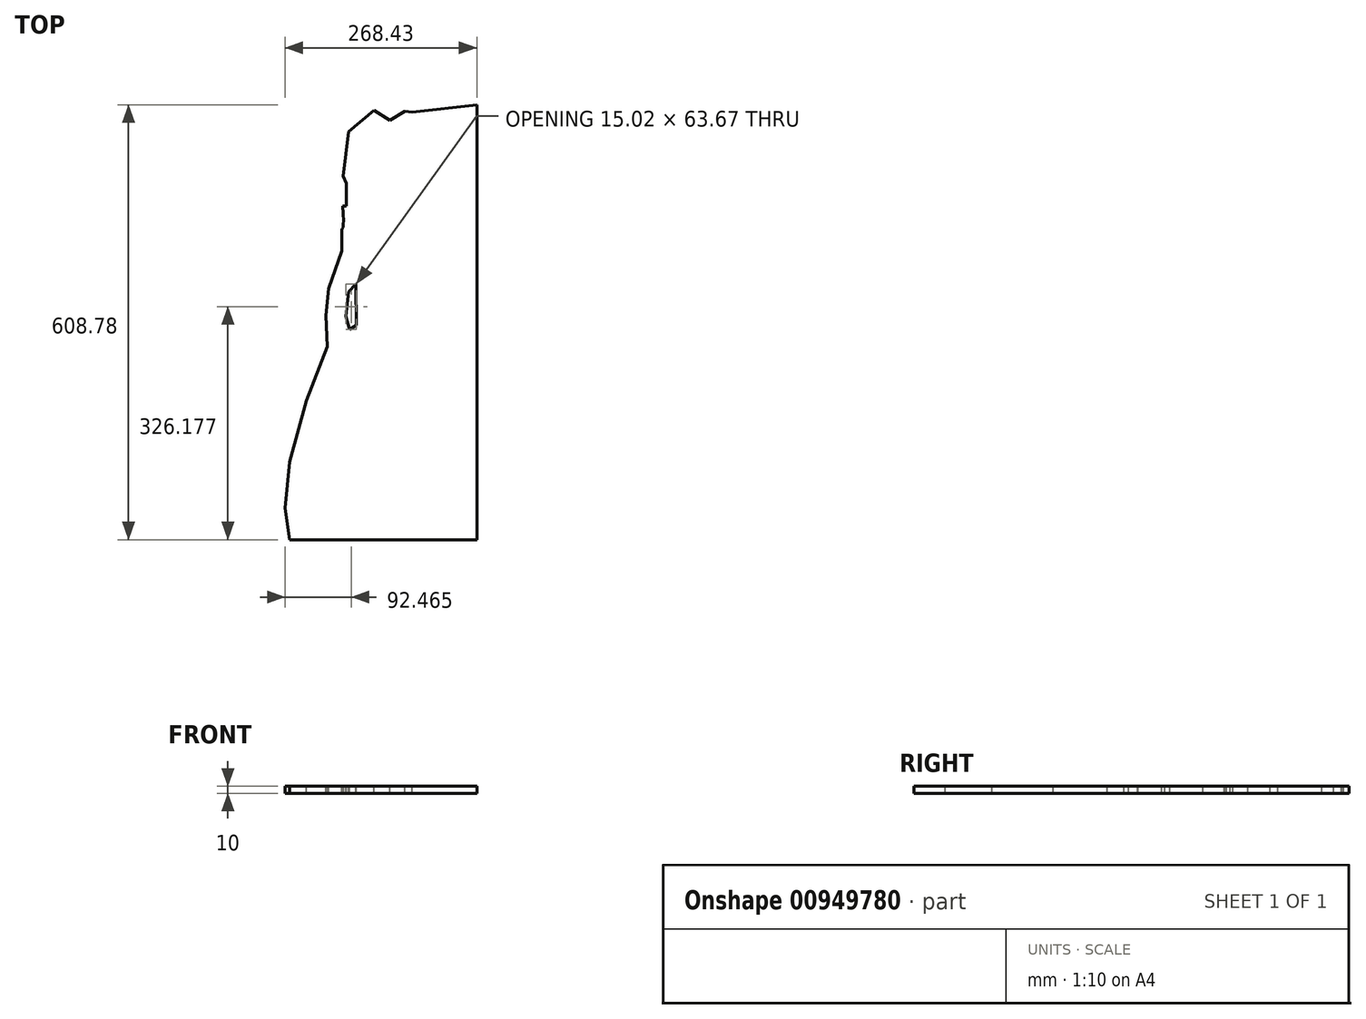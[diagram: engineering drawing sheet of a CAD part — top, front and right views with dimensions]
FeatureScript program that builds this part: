
annotation { "Feature Type Name" : "Feature", "Feature Type Description" : "" }
export const myFeature = defineFeature(function(context is Context, id is Id, definition is map)
    precondition{}
    {
        {
            var Q0;
            Q0=qCreatedBy(makeId("Top.planeOp"),FACE);
            var sketch = newSketch(context, id + "F0", { "sketchPlane" : qUnion([Q0])});
            skLineSegment(sketch, "E0", {"start": v(0, 0) * mm, "end": v(0, 507.42) * mm});
            skLineSegment(sketch, "E1", {"start": v(0, 0) * mm, "end": v(0, -560.7) * mm});
            skLineSegment(sketch, "E2", {"start": v(0, 266.98) * mm, "end": v(-90.5, 256.7) * mm});
            skLineSegment(sketch, "E3", {"start": v(-90.5, 256.7) * mm, "end": v(-100.8, 258.43) * mm});
            skLineSegment(sketch, "E4", {"start": v(-100.8, 258.43) * mm, "end": v(-121.81, 245.63) * mm});
            skLineSegment(sketch, "E5", {"start": v(-121.81, 245.63) * mm, "end": v(-143.96, 259.3) * mm});
            skLineSegment(sketch, "E6", {"start": v(-143.96, 259.3) * mm, "end": v(-179.77, 229.36) * mm});
            skLineSegment(sketch, "E7", {"start": v(-179.77, 229.36) * mm, "end": v(-187.05, 167.53) * mm});
            skLineSegment(sketch, "E8", {"start": v(-187.05, 167.53) * mm, "end": v(-182.93, 157.04) * mm});
            skLineSegment(sketch, "E9", {"start": v(-182.93, 157.04) * mm, "end": v(-182.93, 125.57) * mm});
            skLineSegment(sketch, "E10", {"start": v(-182.93, 125.57) * mm, "end": v(-188, 125.57) * mm});
            skLineSegment(sketch, "E11", {"start": v(-188, 125.57) * mm, "end": v(-187.05, 114.34) * mm});
            skLineSegment(sketch, "E12", {"start": v(-187.05, 114.34) * mm, "end": v(-186.28, 104.53) * mm});
            skLineSegment(sketch, "E13", {"start": v(-186.28, 104.53) * mm, "end": v(-187.05, 100.89) * mm});
            skLineSegment(sketch, "E14", {"start": v(-187.05, 100.89) * mm, "end": v(-187.05, 95.58) * mm});
            skLineSegment(sketch, "E15", {"start": v(-187.05, 95.58) * mm, "end": v(-188.28, 93.74) * mm});
            skLineSegment(sketch, "E16", {"start": v(-189.28, 62.57) * mm, "end": v(-189.28, 92.41) * mm});
            skLineSegment(sketch, "E17", {"start": v(-189.28, 92.41) * mm, "end": v(-188.28, 93.74) * mm});
            skLineSegment(sketch, "E18", {"start": v(-189.28, 62.57) * mm, "end": v(-207.18, 9.6) * mm});
            skLineSegment(sketch, "E19", {"start": v(-207.18, 9.6) * mm, "end": v(-211.46, -27.83) * mm});
            skLineSegment(sketch, "E20", {"start": v(-211.46, -27.83) * mm, "end": v(-209.5, -71.38) * mm});
            skLineSegment(sketch, "E21", {"start": v(-209.5, -71.38) * mm, "end": v(-238.46, -147.05) * mm});
            skLineSegment(sketch, "E22", {"start": v(-238.46, -147.05) * mm, "end": v(-262.31, -232.57) * mm});
            skLineSegment(sketch, "E23", {"start": v(-262.31, -232.57) * mm, "end": v(-268.43, -297.65) * mm});
            skLineSegment(sketch, "E24", {"start": v(-268.43, -297.65) * mm, "end": v(-262.31, -341.8) * mm});
            skLineSegment(sketch, "E25", {"start": v(-262.31, -341.8) * mm, "end": v(0, -341.8) * mm});
            skArc(sketch, "E26", {"start": v(0, 183.04) * mm, "mid": v(-31.78, 179.78) * mm, "end": v(-63.3, 174.56) * mm});
            skLineSegment(sketch, "E27", {"start": v(-63.3, 174.56) * mm, "end": v(-90.15, 159.72) * mm});
            skLineSegment(sketch, "E28", {"start": v(-90.15, 159.72) * mm, "end": v(-110.08, 125.1) * mm});
            skLineSegment(sketch, "E29", {"start": v(-110.08, 125.1) * mm, "end": v(-117.57, 112.44) * mm});
            skLineSegment(sketch, "E30", {"start": v(-117.57, 112.44) * mm, "end": v(-121.54, 81.78) * mm});
            skLineSegment(sketch, "E31", {"start": v(-118.27, 18.78) * mm, "end": v(-121.54, 81.78) * mm});
            skLineSegment(sketch, "E32", {"start": v(-118.27, 18.78) * mm, "end": v(-91.05, -12.19) * mm});
            skLineSegment(sketch, "E33", {"start": v(-91.05, -12.19) * mm, "end": v(-67.19, -36.05) * mm});
            skLineSegment(sketch, "E34", {"start": v(-67.19, -36.05) * mm, "end": v(-44.56, -45.31) * mm});
            skLineSegment(sketch, "E35", {"start": v(-44.56, -45.31) * mm, "end": v(0, -56) * mm});
            skLineSegment(sketch, "E36", {"start": v(-169.38, 16.21) * mm, "end": v(-179.36, 5.2) * mm});
            skLineSegment(sketch, "E37", {"start": v(-179.36, 5.2) * mm, "end": v(-183.47, -28.84) * mm});
            skLineSegment(sketch, "E38", {"start": v(-183.47, -28.84) * mm, "end": v(-178.54, -47.46) * mm});
            skLineSegment(sketch, "E39", {"start": v(-178.54, -47.46) * mm, "end": v(-168.46, -41.7) * mm});
            skLineSegment(sketch, "E40", {"start": v(-168.46, -41.7) * mm, "end": v(-169.38, 16.21) * mm});
            skLineSegment(sketch, "E41", {"start": v(-44.56, 261.84) * mm, "end": v(-91.08, 211.7) * mm});
            skPoint(sketch, "E41.startSnap0", {"position": v(-45.25, 261.84) * mm});
            skLineSegment(sketch, "E42", {"start": v(-91.08, 211.7) * mm, "end": v(-91.08, 200.93) * mm});
            skLineSegment(sketch, "E43", {"start": v(-91.08, 200.93) * mm, "end": v(0, 200.93) * mm});
            skLineSegment(sketch, "E44", {"start": v(0, 200.93) * mm, "end": v(-44.56, 261.84) * mm});
            skLineSegment(sketch, "E45", {"start": v(-153.96, 177.08) * mm, "end": v(-128.27, 176.1) * mm});
            skLineSegment(sketch, "E46", {"start": v(-128.27, 176.1) * mm, "end": v(-128.27, 162.4) * mm});
            skLineSegment(sketch, "E47", {"start": v(-128.27, 162.4) * mm, "end": v(-155.67, 161.42) * mm});
            skLineSegment(sketch, "E48", {"start": v(-155.67, 161.42) * mm, "end": v(-153.96, 177.08) * mm});
            skLineSegment(sketch, "E49", {"start": v(-153.96, 177.08) * mm, "end": v(-128.27, 162.4) * mm});
            skLineSegment(sketch, "E50", {"start": v(-91.08, 200.93) * mm, "end": v(-126.27, 156.06) * mm});
            skLineSegment(sketch, "E51", {"start": v(-126.27, 156.06) * mm, "end": v(-126.27, 98.25) * mm});
            skLineSegment(sketch, "E52", {"start": v(-126.27, 98.25) * mm, "end": v(-117.57, 112.44) * mm});
            skLineSegment(sketch, "E53", {"start": v(-91.08, 200.93) * mm, "end": v(-90.15, 159.72) * mm});
            skLineSegment(sketch, "E54", {"start": v(-63.3, 174.56) * mm, "end": v(-91.08, 200.93) * mm});
            skLineSegment(sketch, "E55", {"start": v(-63.3, 174.56) * mm, "end": v(-45.54, 200.93) * mm});
            skLineSegment(sketch, "E56", {"start": v(-45.54, 200.93) * mm, "end": v(-24.26, 180.73) * mm});
            skLineSegment(sketch, "E57", {"start": v(-91.08, 200.93) * mm, "end": v(-52.43, 253.36) * mm});
            skLineSegment(sketch, "E58", {"start": v(-91.08, 200.93) * mm, "end": v(-26.3, 236.9) * mm});
            skLineSegment(sketch, "E59", {"start": v(-26.3, 236.9) * mm, "end": v(-45.54, 200.93) * mm});
            skLineSegment(sketch, "E60", {"start": v(-90.5, 256.7) * mm, "end": v(-90.5, 236.9) * mm});
            skLineSegment(sketch, "E61", {"start": v(-90.5, 236.9) * mm, "end": v(-67.7, 236.9) * mm});
            skLineSegment(sketch, "E62", {"start": v(-90.5, 236.9) * mm, "end": v(-121.53, 235.06) * mm});
            skLineSegment(sketch, "E63", {"start": v(-121.53, 235.06) * mm, "end": v(-91.08, 211.7) * mm});
            skLineSegment(sketch, "E64", {"start": v(-100.8, 258.43) * mm, "end": v(-121.53, 235.06) * mm});
            skLineSegment(sketch, "E65", {"start": v(-121.53, 235.06) * mm, "end": v(-136.76, 246.17) * mm});
            skLineSegment(sketch, "E66", {"start": v(-136.76, 246.17) * mm, "end": v(-160.62, 230.94) * mm});
            skLineSegment(sketch, "E67", {"start": v(-160.62, 230.94) * mm, "end": v(-121.53, 235.06) * mm});
            skLineSegment(sketch, "E68", {"start": v(-136.76, 246.17) * mm, "end": v(-136.76, 233.45) * mm});
            skLineSegment(sketch, "E69", {"start": v(-143.96, 259.3) * mm, "end": v(-160.62, 230.94) * mm});
            skLineSegment(sketch, "E70", {"start": v(-160.62, 230.94) * mm, "end": v(-170.75, 236.9) * mm});
            skLineSegment(sketch, "E71", {"start": v(-160.62, 230.94) * mm, "end": v(-183.13, 200.78) * mm});
            skLineSegment(sketch, "E72", {"start": v(-183.13, 200.78) * mm, "end": v(-160.62, 200.78) * mm});
            skLineSegment(sketch, "E73", {"start": v(-160.62, 200.78) * mm, "end": v(-160.62, 230.94) * mm});
            skLineSegment(sketch, "E74", {"start": v(-160.62, 200.78) * mm, "end": v(-160.62, 180.95) * mm});
            skLineSegment(sketch, "E75", {"start": v(-160.62, 180.95) * mm, "end": v(-183.13, 200.78) * mm});
            skLineSegment(sketch, "E76", {"start": v(-160.62, 180.95) * mm, "end": v(-122.97, 180.95) * mm});
            skLineSegment(sketch, "E77", {"start": v(-122.97, 180.95) * mm, "end": v(-119.68, 201.32) * mm});
            skLineSegment(sketch, "E78", {"start": v(-119.68, 201.32) * mm, "end": v(-160.62, 180.95) * mm});
            skLineSegment(sketch, "E79", {"start": v(-119.68, 201.32) * mm, "end": v(-118.1, 214.75) * mm});
            skLineSegment(sketch, "E80", {"start": v(-118.1, 214.75) * mm, "end": v(-91.08, 211.7) * mm});
            skLineSegment(sketch, "E81", {"start": v(-164.1, 184.02) * mm, "end": v(-183.13, 171.67) * mm});
            skLineSegment(sketch, "E82", {"start": v(-183.13, 171.67) * mm, "end": v(-182.93, 157.04) * mm});
            skLineSegment(sketch, "E83", {"start": v(-155.67, 161.42) * mm, "end": v(-145.46, 109.55) * mm});
            skLineSegment(sketch, "E84", {"start": v(-145.46, 109.55) * mm, "end": v(-126.27, 156.06) * mm});
            skLineSegment(sketch, "E85", {"start": v(-126.27, 156.06) * mm, "end": v(-155.67, 161.42) * mm});
            skLineSegment(sketch, "E86", {"start": v(-182.93, 125.57) * mm, "end": v(-167.94, 117) * mm});
            skLineSegment(sketch, "E87", {"start": v(-167.94, 117) * mm, "end": v(-161, 122.74) * mm});
            skLineSegment(sketch, "E88", {"start": v(-161, 122.74) * mm, "end": v(-145.46, 109.55) * mm});
            skLineSegment(sketch, "E89", {"start": v(-161, 122.74) * mm, "end": v(-158.39, 94.84) * mm});
            skLineSegment(sketch, "E90", {"start": v(-158.39, 94.84) * mm, "end": v(-145.46, 109.55) * mm});
            skLineSegment(sketch, "E91", {"start": v(-167.94, 117) * mm, "end": v(-167.94, 83.06) * mm});
            skLineSegment(sketch, "E92", {"start": v(-167.94, 83.06) * mm, "end": v(-126.27, 98.25) * mm});
            skLineSegment(sketch, "E93", {"start": v(-126.27, 98.25) * mm, "end": v(-145.46, 109.55) * mm});
            skLineSegment(sketch, "E94", {"start": v(-167.94, 83.06) * mm, "end": v(-149.47, 69.65) * mm});
            skLineSegment(sketch, "E95", {"start": v(-149.47, 69.65) * mm, "end": v(-149.47, 83.06) * mm});
            skLineSegment(sketch, "E96", {"start": v(-149.47, 83.06) * mm, "end": v(-167.94, 83.06) * mm});
            skLineSegment(sketch, "E97", {"start": v(-149.47, 83.06) * mm, "end": v(-121.54, 81.78) * mm});
            skLineSegment(sketch, "E98", {"start": v(-121.54, 81.78) * mm, "end": v(-137.06, 74.86) * mm});
            skLineSegment(sketch, "E99", {"start": v(-137.06, 74.86) * mm, "end": v(-149.47, 83.06) * mm});
            skLineSegment(sketch, "E100", {"start": v(-137.06, 74.86) * mm, "end": v(-141.3, 50.8) * mm});
            skLineSegment(sketch, "E101", {"start": v(-141.3, 50.8) * mm, "end": v(-149.47, 83.06) * mm});
            skLineSegment(sketch, "E102", {"start": v(-189.28, 62.57) * mm, "end": v(-167.94, 83.06) * mm});
            skLineSegment(sketch, "E103", {"start": v(-189.28, 62.57) * mm, "end": v(-167.94, 61.6) * mm});
            skLineSegment(sketch, "E104", {"start": v(-167.94, 61.6) * mm, "end": v(-159.08, 76.63) * mm});
            skLineSegment(sketch, "E105", {"start": v(-167.94, 61.6) * mm, "end": v(-149.47, 69.65) * mm});
            skLineSegment(sketch, "E106", {"start": v(-155.63, 66.97) * mm, "end": v(-142.35, 43.46) * mm});
            skLineSegment(sketch, "E107", {"start": v(-142.35, 43.46) * mm, "end": v(-146.97, 19.46) * mm});
            skLineSegment(sketch, "E108", {"start": v(-146.97, 19.46) * mm, "end": v(-120.59, 63.43) * mm});
            skLineSegment(sketch, "E109", {"start": v(-120.59, 63.43) * mm, "end": v(-137.06, 74.86) * mm});
            skLineSegment(sketch, "E110", {"start": v(-146.97, 19.46) * mm, "end": v(-118.27, 18.78) * mm});
            skLineSegment(sketch, "E111", {"start": v(-167.94, 61.6) * mm, "end": v(-158.47, 43.27) * mm});
            skLineSegment(sketch, "E112", {"start": v(-158.47, 43.27) * mm, "end": v(-189.28, 62.57) * mm});
            skLineSegment(sketch, "E113", {"start": v(-189.28, 62.57) * mm, "end": v(-176.46, 37.86) * mm});
            skLineSegment(sketch, "E114", {"start": v(-176.46, 37.86) * mm, "end": v(-198, 36.75) * mm});
            skLineSegment(sketch, "E115", {"start": v(-198, 36.75) * mm, "end": v(-179.36, 5.2) * mm});
            skLineSegment(sketch, "E116", {"start": v(-169.38, 16.21) * mm, "end": v(-167.06, 18.78) * mm});
            skLineSegment(sketch, "E117", {"start": v(-167.06, 18.78) * mm, "end": v(-160.56, 3.9) * mm});
            skLineSegment(sketch, "E118", {"start": v(-160.56, 3.9) * mm, "end": v(-135.06, 7.39) * mm});
            skLineSegment(sketch, "E119", {"start": v(-135.06, 7.39) * mm, "end": v(-146.97, 19.46) * mm});
            skLineSegment(sketch, "E120", {"start": v(-160.56, 3.9) * mm, "end": v(-151.17, 27.66) * mm});
            skLineSegment(sketch, "E121", {"start": v(-151.17, 27.66) * mm, "end": v(-167.06, 18.78) * mm});
            skLineSegment(sketch, "E122", {"start": v(-167.06, 18.78) * mm, "end": v(-154.98, 34.8) * mm});
            skLineSegment(sketch, "E123", {"start": v(-154.98, 34.8) * mm, "end": v(-151.17, 27.66) * mm});
            skLineSegment(sketch, "E124", {"start": v(-168.88, -15.09) * mm, "end": v(-160.56, 3.9) * mm});
            skLineSegment(sketch, "E125", {"start": v(-207.18, 9.6) * mm, "end": v(-179.36, 5.2) * mm});
            skLineSegment(sketch, "E126", {"start": v(-207.18, 9.6) * mm, "end": v(-193.24, -10.33) * mm});
            skLineSegment(sketch, "E127", {"start": v(-193.24, -10.33) * mm, "end": v(-211.46, -27.83) * mm});
            skLineSegment(sketch, "E128", {"start": v(-211.46, -27.83) * mm, "end": v(-192.85, -44.71) * mm});
            skLineSegment(sketch, "E129", {"start": v(-192.85, -44.71) * mm, "end": v(-209.5, -71.38) * mm});
            skLineSegment(sketch, "E130", {"start": v(-209.5, -71.38) * mm, "end": v(-178.54, -47.46) * mm});
            skLineSegment(sketch, "E131", {"start": v(-178.54, -47.46) * mm, "end": v(-191.28, -85.19) * mm});
            skLineSegment(sketch, "E132", {"start": v(-191.28, -85.19) * mm, "end": v(-104, -43.18) * mm});
            skLineSegment(sketch, "E133", {"start": v(-104, -43.18) * mm, "end": v(-121.28, -16.12) * mm});
            skLineSegment(sketch, "E134", {"start": v(-121.28, -16.12) * mm, "end": v(-132.5, -15.85) * mm});
            skLineSegment(sketch, "E135", {"start": v(-132.5, -15.85) * mm, "end": v(-168.46, -41.7) * mm});
            skLineSegment(sketch, "E136", {"start": v(-132.5, -15.85) * mm, "end": v(-160.56, 3.9) * mm});
            skLineSegment(sketch, "E137", {"start": v(-135.06, 7.39) * mm, "end": v(-121.28, -16.12) * mm});
            skLineSegment(sketch, "E138", {"start": v(-135.06, 7.39) * mm, "end": v(-118.27, -7.83) * mm});
            skLineSegment(sketch, "E139", {"start": v(-118.27, -7.83) * mm, "end": v(-134.51, 19.16) * mm});
            skLineSegment(sketch, "E140", {"start": v(-124.6, 18.93) * mm, "end": v(-118.27, -7.83) * mm});
            skLineSegment(sketch, "E141", {"start": v(-118.27, 18.78) * mm, "end": v(-111.8, 0) * mm});
            skLineSegment(sketch, "E142", {"start": v(-111.8, 0) * mm, "end": v(-118.27, -7.83) * mm});
            skLineSegment(sketch, "E143", {"start": v(-118.27, -7.83) * mm, "end": v(-97.61, -32.76) * mm});
            skLineSegment(sketch, "E144", {"start": v(-97.61, -32.76) * mm, "end": v(-96.23, -17.19) * mm});
            skLineSegment(sketch, "E145", {"start": v(-96.23, -17.19) * mm, "end": v(-111.8, 0) * mm});
            skLineSegment(sketch, "E146", {"start": v(-96.23, -17.19) * mm, "end": v(-70.86, -40.2) * mm});
            skLineSegment(sketch, "E147", {"start": v(-70.86, -40.2) * mm, "end": v(-97.61, -32.76) * mm});
            skLineSegment(sketch, "E148", {"start": v(-115.17, -25.68) * mm, "end": v(-109.06, -18.94) * mm});
            skLineSegment(sketch, "E149", {"start": v(-104, -43.18) * mm, "end": v(-90.9, -41.74) * mm});
            skLineSegment(sketch, "E150", {"start": v(-90.9, -41.74) * mm, "end": v(-97.61, -32.76) * mm});
            skLineSegment(sketch, "E151", {"start": v(-191.28, -85.19) * mm, "end": v(-223.98, -109.21) * mm});
            skLineSegment(sketch, "E152", {"start": v(-223.98, -109.21) * mm, "end": v(-199.44, -142.62) * mm});
            skLineSegment(sketch, "E153", {"start": v(-199.44, -142.62) * mm, "end": v(-180.83, -164.7) * mm});
            skLineSegment(sketch, "E154", {"start": v(-180.83, -164.7) * mm, "end": v(-244.2, -235.13) * mm});
            skLineSegment(sketch, "E155", {"start": v(-244.2, -235.13) * mm, "end": v(-244.2, -167.65) * mm});
            skLineSegment(sketch, "E156", {"start": v(-244.2, -167.65) * mm, "end": v(-199.44, -142.62) * mm});
            skLineSegment(sketch, "E157", {"start": v(-180.83, -164.7) * mm, "end": v(-178.17, -127.86) * mm});
            skLineSegment(sketch, "E158", {"start": v(-178.17, -127.86) * mm, "end": v(-191.28, -85.19) * mm});
            skLineSegment(sketch, "E159", {"start": v(-178.17, -127.86) * mm, "end": v(-104, -83.23) * mm});
            skLineSegment(sketch, "E160", {"start": v(-104, -83.23) * mm, "end": v(-191.28, -85.19) * mm});
            skLineSegment(sketch, "E161", {"start": v(-104, -83.23) * mm, "end": v(-104, -43.18) * mm});
            skLineSegment(sketch, "E162", {"start": v(-104, -83.23) * mm, "end": v(-73.4, -63.7) * mm});
            skLineSegment(sketch, "E163", {"start": v(-73.4, -63.7) * mm, "end": v(-90.9, -41.74) * mm});
            skLineSegment(sketch, "E164", {"start": v(-70.86, -40.2) * mm, "end": v(-73.4, -63.7) * mm});
            skLineSegment(sketch, "E165", {"start": v(-73.4, -63.7) * mm, "end": v(-35.39, -65.04) * mm});
            skLineSegment(sketch, "E166", {"start": v(-35.39, -65.04) * mm, "end": v(0, -64.25) * mm});
            skLineSegment(sketch, "E167", {"start": v(-73.4, -63.7) * mm, "end": v(-56.14, -99.54) * mm});
            skLineSegment(sketch, "E168", {"start": v(-56.14, -99.54) * mm, "end": v(-35.39, -65.04) * mm});
            skLineSegment(sketch, "E169", {"start": v(-56.14, -99.54) * mm, "end": v(-18.87, -80.3) * mm});
            skLineSegment(sketch, "E170", {"start": v(-18.87, -80.3) * mm, "end": v(0, -98.53) * mm});
            skLineSegment(sketch, "E171", {"start": v(0, -98.53) * mm, "end": v(-56.14, -99.54) * mm});
            skLineSegment(sketch, "E172", {"start": v(-35.39, -88.83) * mm, "end": v(-18.75, -96.45) * mm});
            skLineSegment(sketch, "E173", {"start": v(-18.75, -96.45) * mm, "end": v(-37.95, -97.8) * mm});
            skLineSegment(sketch, "E174", {"start": v(-37.95, -97.8) * mm, "end": v(-35.39, -88.83) * mm});
            skLineSegment(sketch, "E175", {"start": v(-18.75, -96.45) * mm, "end": v(-18.87, -80.3) * mm});
            skLineSegment(sketch, "E176", {"start": v(-56.14, -99.54) * mm, "end": v(-104, -83.23) * mm});
            skLineSegment(sketch, "E177", {"start": v(-56.14, -99.54) * mm, "end": v(-9.08, -110.76) * mm});
            skLineSegment(sketch, "E178", {"start": v(-9.08, -110.76) * mm, "end": v(0, -112.35) * mm});
            skLineSegment(sketch, "E179", {"start": v(-178.17, -127.86) * mm, "end": v(-132.63, -176.2) * mm});
            skLineSegment(sketch, "E180", {"start": v(-132.63, -176.2) * mm, "end": v(-112.88, -132.17) * mm});
            skLineSegment(sketch, "E181", {"start": v(-112.88, -132.17) * mm, "end": v(-104, -83.23) * mm});
            skLineSegment(sketch, "E182", {"start": v(-112.88, -132.17) * mm, "end": v(-56.14, -99.54) * mm});
            skLineSegment(sketch, "E183", {"start": v(-112.88, -132.17) * mm, "end": v(-90.84, -184.26) * mm});
            skLineSegment(sketch, "E184", {"start": v(-90.84, -184.26) * mm, "end": v(-75.1, -161.42) * mm});
            skLineSegment(sketch, "E185", {"start": v(-75.1, -161.42) * mm, "end": v(-76.23, -111.1) * mm});
            skLineSegment(sketch, "E186", {"start": v(-76.23, -111.1) * mm, "end": v(-60.57, -172.32) * mm});
            skLineSegment(sketch, "E187", {"start": v(-60.57, -172.32) * mm, "end": v(-73.4, -194.12) * mm});
            skLineSegment(sketch, "E188", {"start": v(-73.4, -194.12) * mm, "end": v(-75.1, -161.42) * mm});
            skLineSegment(sketch, "E189", {"start": v(-60.57, -172.32) * mm, "end": v(-56.14, -99.54) * mm});
            skLineSegment(sketch, "E190", {"start": v(-9.08, -110.76) * mm, "end": v(-8.33, -173.02) * mm});
            skLineSegment(sketch, "E191", {"start": v(-8.33, -173.02) * mm, "end": v(-12.48, -185.3) * mm});
            skLineSegment(sketch, "E192", {"start": v(-12.48, -185.3) * mm, "end": v(0, -175.1) * mm});
            skLineSegment(sketch, "E193", {"start": v(-12.48, -185.3) * mm, "end": v(-31.84, -161.63) * mm});
            skLineSegment(sketch, "E194", {"start": v(-31.84, -161.63) * mm, "end": v(-60.57, -172.32) * mm});
            skLineSegment(sketch, "E195", {"start": v(-31.84, -161.63) * mm, "end": v(-30.07, -195.33) * mm});
            skLineSegment(sketch, "E196", {"start": v(-30.07, -195.33) * mm, "end": v(-12.48, -185.3) * mm});
            skLineSegment(sketch, "E197", {"start": v(-12.48, -185.3) * mm, "end": v(0, -189.52) * mm});
            skLineSegment(sketch, "E198", {"start": v(-244.2, -235.13) * mm, "end": v(-262.31, -232.57) * mm});
            skLineSegment(sketch, "E199", {"start": v(-244.2, -235.13) * mm, "end": v(-222.72, -236.44) * mm});
            skLineSegment(sketch, "E200", {"start": v(-222.72, -236.44) * mm, "end": v(-186.97, -307.64) * mm});
            skLineSegment(sketch, "E201", {"start": v(-186.97, -307.64) * mm, "end": v(-165, -237.38) * mm});
            skLineSegment(sketch, "E202", {"start": v(-165, -237.38) * mm, "end": v(-222.72, -236.44) * mm});
            skLineSegment(sketch, "E203", {"start": v(-165, -237.38) * mm, "end": v(-104.63, -238.55) * mm});
            skLineSegment(sketch, "E204", {"start": v(-104.63, -238.55) * mm, "end": v(-115.28, -272.62) * mm});
            skLineSegment(sketch, "E205", {"start": v(-115.28, -272.62) * mm, "end": v(-186.97, -307.64) * mm});
            skLineSegment(sketch, "E206", {"start": v(-165, -237.38) * mm, "end": v(-132.63, -176.2) * mm});
            skLineSegment(sketch, "E207", {"start": v(-162.45, -232.57) * mm, "end": v(-219.06, -207.18) * mm});
            skLineSegment(sketch, "E208", {"start": v(-162.45, -232.57) * mm, "end": v(-108.31, -207) * mm});
            skLineSegment(sketch, "E209", {"start": v(-108.31, -207) * mm, "end": v(-132.63, -176.2) * mm});
            skLineSegment(sketch, "E210", {"start": v(-108.31, -207) * mm, "end": v(-104.63, -238.55) * mm});
            skLineSegment(sketch, "E211", {"start": v(-108.31, -207) * mm, "end": v(-90.84, -184.26) * mm});
            skLineSegment(sketch, "E212", {"start": v(-73.4, -194.12) * mm, "end": v(-90.84, -184.26) * mm});
            skLineSegment(sketch, "E213", {"start": v(-73.4, -194.12) * mm, "end": v(-108.31, -207) * mm});
            skLineSegment(sketch, "E214", {"start": v(-104.63, -238.55) * mm, "end": v(-100.85, -225) * mm});
            skLineSegment(sketch, "E215", {"start": v(-100.85, -225) * mm, "end": v(-73.4, -194.12) * mm});
            skLineSegment(sketch, "E216", {"start": v(-268.43, -297.65) * mm, "end": v(-222.72, -236.44) * mm});
            skLineSegment(sketch, "E217", {"start": v(-186.97, -307.64) * mm, "end": v(-225.46, -326.97) * mm});
            skLineSegment(sketch, "E218", {"start": v(-225.46, -326.97) * mm, "end": v(-268.43, -297.65) * mm});
            skLineSegment(sketch, "E219", {"start": v(-225.46, -326.97) * mm, "end": v(-203.24, -341.8) * mm});
            skLineSegment(sketch, "E220", {"start": v(-203.24, -341.8) * mm, "end": v(-147.32, -288.28) * mm});
            skLineSegment(sketch, "E221", {"start": v(-147.32, -288.28) * mm, "end": v(-138.65, -341.8) * mm});
            skLineSegment(sketch, "E222", {"start": v(-138.65, -341.8) * mm, "end": v(-105.86, -277.23) * mm});
            skLineSegment(sketch, "E223", {"start": v(-105.86, -277.23) * mm, "end": v(-115.28, -272.62) * mm});
            skLineSegment(sketch, "E224", {"start": v(-117.47, -341.8) * mm, "end": v(-100.85, -292.66) * mm});
            skLineSegment(sketch, "E225", {"start": v(-100.85, -292.66) * mm, "end": v(-110.98, -287.3) * mm});
            skLineSegment(sketch, "E226", {"start": v(-110.98, -287.3) * mm, "end": v(-69.33, -272.62) * mm});
            skLineSegment(sketch, "E227", {"start": v(-69.33, -272.62) * mm, "end": v(-53.29, -289.16) * mm});
            skLineSegment(sketch, "E228", {"start": v(-53.29, -289.16) * mm, "end": v(-67.68, -305.16) * mm});
            skLineSegment(sketch, "E229", {"start": v(-67.68, -305.16) * mm, "end": v(-100.85, -292.66) * mm});
            skLineSegment(sketch, "E230", {"start": v(-117.47, -341.8) * mm, "end": v(-67.68, -305.16) * mm});
            skLineSegment(sketch, "E231", {"start": v(-67.68, -305.16) * mm, "end": v(-73.4, -341.8) * mm});
            skLineSegment(sketch, "E232", {"start": v(-105.86, -277.23) * mm, "end": v(-91.4, -247.7) * mm});
            skLineSegment(sketch, "E233", {"start": v(-91.4, -247.7) * mm, "end": v(-104.63, -238.55) * mm});
            skLineSegment(sketch, "E234", {"start": v(-91.4, -247.7) * mm, "end": v(-91.4, -240.67) * mm});
            skLineSegment(sketch, "E235", {"start": v(-91.4, -240.67) * mm, "end": v(-100.85, -225) * mm});
            skLineSegment(sketch, "E236", {"start": v(-73.4, -194.12) * mm, "end": v(-91.4, -240.67) * mm});
            skLineSegment(sketch, "E237", {"start": v(-91.4, -247.7) * mm, "end": v(-65.56, -207.94) * mm});
            skLineSegment(sketch, "E238", {"start": v(-65.56, -207.94) * mm, "end": v(-73.4, -194.12) * mm});
            skLineSegment(sketch, "E239", {"start": v(-65.56, -207.94) * mm, "end": v(-51.2, -233.29) * mm});
            skLineSegment(sketch, "E240", {"start": v(-51.2, -233.29) * mm, "end": v(-36.58, -219.38) * mm});
            skLineSegment(sketch, "E241", {"start": v(-36.58, -219.38) * mm, "end": v(-60.57, -172.32) * mm});
            skLineSegment(sketch, "E242", {"start": v(-69.33, -272.62) * mm, "end": v(-51.2, -233.29) * mm});
            skLineSegment(sketch, "E243", {"start": v(-91.4, -247.7) * mm, "end": v(-51.2, -233.29) * mm});
            skLineSegment(sketch, "E244", {"start": v(-36.58, -219.38) * mm, "end": v(-30.07, -195.33) * mm});
            skLineSegment(sketch, "E245", {"start": v(-30.07, -195.33) * mm, "end": v(-46.23, -166.99) * mm});
            skLineSegment(sketch, "E246", {"start": v(-30.07, -195.33) * mm, "end": v(0, -209.16) * mm});
            skLineSegment(sketch, "E247", {"start": v(0, -209.16) * mm, "end": v(-24.48, -209.16) * mm});
            skLineSegment(sketch, "E248", {"start": v(-24.48, -209.16) * mm, "end": v(-36.58, -219.38) * mm});
            skLineSegment(sketch, "E249", {"start": v(-51.2, -233.29) * mm, "end": v(-26.2, -247.4) * mm});
            skLineSegment(sketch, "E250", {"start": v(-26.2, -247.4) * mm, "end": v(-11.34, -244.45) * mm});
            skLineSegment(sketch, "E251", {"start": v(-11.34, -244.45) * mm, "end": v(-18.43, -221.27) * mm});
            skLineSegment(sketch, "E252", {"start": v(-18.43, -221.27) * mm, "end": v(-36.58, -219.38) * mm});
            skLineSegment(sketch, "E253", {"start": v(-18.43, -221.27) * mm, "end": v(-19.06, -209.16) * mm});
            skLineSegment(sketch, "E254", {"start": v(-18.43, -221.27) * mm, "end": v(0, -209.16) * mm});
            skLineSegment(sketch, "E255", {"start": v(-18.43, -221.27) * mm, "end": v(0, -220.3) * mm});
            skLineSegment(sketch, "E256", {"start": v(-18.43, -221.27) * mm, "end": v(0, -235.28) * mm});
            skLineSegment(sketch, "E257", {"start": v(0, -235.28) * mm, "end": v(-11.34, -244.45) * mm});
            skLineSegment(sketch, "E258", {"start": v(-11.34, -244.45) * mm, "end": v(-5.73, -254.35) * mm});
            skLineSegment(sketch, "E259", {"start": v(-5.73, -254.35) * mm, "end": v(0, -260.37) * mm});
            skLineSegment(sketch, "E260", {"start": v(-69.33, -272.62) * mm, "end": v(-36.78, -253.37) * mm});
            skLineSegment(sketch, "E261", {"start": v(-36.78, -253.37) * mm, "end": v(-51.2, -233.29) * mm});
            skLineSegment(sketch, "E262", {"start": v(-36.78, -253.37) * mm, "end": v(-26.2, -247.4) * mm});
            skLineSegment(sketch, "E263", {"start": v(-26.2, -247.4) * mm, "end": v(-16.65, -264.35) * mm});
            skLineSegment(sketch, "E264", {"start": v(-16.65, -264.35) * mm, "end": v(-5.73, -254.35) * mm});
            skLineSegment(sketch, "E265", {"start": v(-9.87, -258.14) * mm, "end": v(0, -276.1) * mm});
            skLineSegment(sketch, "E266", {"start": v(0, -278.67) * mm, "end": v(-16.65, -264.35) * mm});
            skLineSegment(sketch, "E267", {"start": v(-16.65, -264.35) * mm, "end": v(-36.78, -253.37) * mm});
            skLineSegment(sketch, "E268", {"start": v(-36.78, -253.37) * mm, "end": v(-35.95, -275.18) * mm});
            skLineSegment(sketch, "E269", {"start": v(-35.95, -275.18) * mm, "end": v(-16.65, -264.35) * mm});
            skLineSegment(sketch, "E270", {"start": v(-35.95, -275.18) * mm, "end": v(-69.33, -272.62) * mm});
            skLineSegment(sketch, "E271", {"start": v(-53.29, -289.16) * mm, "end": v(-35.95, -275.18) * mm});
            skLineSegment(sketch, "E272", {"start": v(-35.95, -275.18) * mm, "end": v(-21.56, -275.45) * mm});
            skLineSegment(sketch, "E273", {"start": v(-21.56, -275.45) * mm, "end": v(-16.65, -264.35) * mm});
            skLineSegment(sketch, "E274", {"start": v(-21.56, -275.45) * mm, "end": v(0, -280.35) * mm});
            skLineSegment(sketch, "E275", {"start": v(-53.29, -289.16) * mm, "end": v(-36.88, -288.05) * mm});
            skLineSegment(sketch, "E276", {"start": v(-36.88, -288.05) * mm, "end": v(-21.56, -275.45) * mm});
            skLineSegment(sketch, "E277", {"start": v(-24.16, -277.6) * mm, "end": v(-24.16, -300.29) * mm});
            skLineSegment(sketch, "E278", {"start": v(-24.16, -300.29) * mm, "end": v(-14.3, -277.1) * mm});
            skLineSegment(sketch, "E279", {"start": v(-36.88, -288.05) * mm, "end": v(-24.16, -300.29) * mm});
            skLineSegment(sketch, "E280", {"start": v(-67.68, -305.16) * mm, "end": v(-36.88, -288.05) * mm});
            skLineSegment(sketch, "E281", {"start": v(-67.68, -305.16) * mm, "end": v(-46.48, -313.8) * mm});
            skLineSegment(sketch, "E282", {"start": v(-46.48, -313.8) * mm, "end": v(-19.51, -305.16) * mm});
            skLineSegment(sketch, "E283", {"start": v(-19.51, -305.16) * mm, "end": v(-24.16, -300.29) * mm});
            skLineSegment(sketch, "E284", {"start": v(-14.3, -277.1) * mm, "end": v(0, -326.68) * mm});
            skLineSegment(sketch, "E285", {"start": v(0, -326.68) * mm, "end": v(-19.51, -305.16) * mm});
            skLineSegment(sketch, "E286", {"start": v(-19.51, -305.16) * mm, "end": v(-25.85, -324.42) * mm});
            skLineSegment(sketch, "E287", {"start": v(-25.85, -324.42) * mm, "end": v(0, -327.56) * mm});
            skLineSegment(sketch, "E288", {"start": v(-46.48, -313.8) * mm, "end": v(-60.6, -318.65) * mm});
            skLineSegment(sketch, "E289", {"start": v(-60.6, -318.65) * mm, "end": v(-25.85, -324.42) * mm});
            skLineSegment(sketch, "E290", {"start": v(-60.6, -318.65) * mm, "end": v(-73.4, -341.8) * mm});
            skLineSegment(sketch, "E291", {"start": v(-73.4, -341.8) * mm, "end": v(-25.85, -324.42) * mm});
            skLineSegment(sketch, "E292", {"start": v(-43.97, -331.04) * mm, "end": v(-49.68, -341.8) * mm});
            skLineSegment(sketch, "E293", {"start": v(-43.97, -331.04) * mm, "end": v(-29.39, -341.8) * mm});
            skLineSegment(sketch, "E294", {"start": v(-29.39, -341.8) * mm, "end": v(0, -327.56) * mm});
            skPoint(sketch, "E295.endSnap0", {"position": v(-246.95, -312.31) * mm});
            skLineSegment(sketch, "E296.trimOffspring", {"start": v(-244.13, -235.04) * mm, "end": v(-244.13, -235.13) * mm});
            skPoint(sketch, "E297.trimOffspring.end.orphan", {"position": v(-246.95, -341.8) * mm});
            skSolve(sketch);
        }
        {
            var Q0;
            Q0=makeQuery(id+"F0.imprint","IMPRINT",FACE,{"disambiguationData":[TD([[makeQuery(id+"F0.imprint","IMPRINT",EDGE,{"derivedFrom":sQuery(id+"F0.wireOp",EDGE,"E177")}),-1.0]])]});
            var Q1;
            {var subQ0=sQuery(id+"F0.wireOp",EDGE,"E241");Q1=makeQuery(id+"F0.imprint","IMPRINT",FACE,{"disambiguationData":[TD([[makeQuery(id+"F0.imprint","IMPRINT",EDGE,{"derivedFrom":subQ0}),-1.0]])]});}
            var Q2;
            {var subQ0=sQuery(id+"F0.wireOp",EDGE,"E230");Q2=makeQuery(id+"F0.imprint","IMPRINT",FACE,{"disambiguationData":[TD([[makeQuery(id+"F0.imprint","IMPRINT",EDGE,{"derivedFrom":subQ0}),-1.0]])]});}
            var Q3;
            Q3=makeQuery(id+"F0.imprint","IMPRINT",FACE,{"disambiguationData":[TD([[makeQuery(id+"F0.imprint","IMPRINT",EDGE,{"derivedFrom":sQuery(id+"F0.wireOp",EDGE,"E151")}),1.0]])]});
            var Q4;
            {var subQ2=sQuery(id+"F0.wireOp",EDGE,"E186");Q4=makeQuery(id+"F0.imprint","IMPRINT",FACE,{"disambiguationData":[TD([[makeQuery(id+"F0.imprint","IMPRINT",EDGE,{"derivedFrom":subQ2}),1.0]])]});}
            var Q5;
            {var subQ4=sQuery(id+"F0.wireOp",EDGE,"E27");Q5=makeQuery(id+"F0.imprint","IMPRINT",FACE,{"disambiguationData":[TD([[makeQuery(id+"F0.imprint","IMPRINT",EDGE,{"derivedFrom":subQ4}),1.0]])]});}
            var Q6;
            {var subQ4=sQuery(id+"F0.wireOp",EDGE,"E153");Q6=makeQuery(id+"F0.imprint","IMPRINT",FACE,{"disambiguationData":[TD([[makeQuery(id+"F0.imprint","IMPRINT",EDGE,{"derivedFrom":subQ4}),-1.0]])]});}
            var Q7;
            {var subQ0=sQuery(id+"F0.wireOp",EDGE,"E226");Q7=makeQuery(id+"F0.imprint","IMPRINT",FACE,{"disambiguationData":[TD([[makeQuery(id+"F0.imprint","IMPRINT",EDGE,{"derivedFrom":subQ0}),1.0]])]});}
            var Q8;
            Q8=makeQuery(id+"F0.imprint","IMPRINT",FACE,{"disambiguationData":[TD([[makeQuery(id+"F0.imprint","IMPRINT",EDGE,{"derivedFrom":sQuery(id+"F0.wireOp",EDGE,"E39")}),-1.0]])]});
            var Q9;
            {var subQ3=sQuery(id+"F0.wireOp",EDGE,"E201");Q9=makeQuery(id+"F0.imprint","IMPRINT",FACE,{"disambiguationData":[TD([[makeQuery(id+"F0.imprint","IMPRINT",EDGE,{"derivedFrom":subQ3}),-1.0]])]});}
            var Q10;
            {var subQ0=sQuery(id+"F0.wireOp",EDGE,"E217");Q10=makeQuery(id+"F0.imprint","IMPRINT",FACE,{"disambiguationData":[TD([[makeQuery(id+"F0.imprint","IMPRINT",EDGE,{"derivedFrom":subQ0}),1.0]])]});}
            var Q11;
            {var subQ3=sQuery(id+"F0.wireOp",EDGE,"E224");Q11=makeQuery(id+"F0.imprint","IMPRINT",FACE,{"disambiguationData":[TD([[makeQuery(id+"F0.imprint","IMPRINT",EDGE,{"derivedFrom":subQ3}),1.0]])]});}
            var Q12;
            Q12=makeQuery(id+"F0.imprint","IMPRINT",FACE,{"disambiguationData":[TD([[makeQuery(id+"F0.imprint","IMPRINT",EDGE,{"derivedFrom":sQuery(id+"F0.wireOp",EDGE,"E159")}),-1.0]])]});
            var Q13;
            Q13=makeQuery(id+"F0.imprint","IMPRINT",FACE,{"disambiguationData":[TD([[makeQuery(id+"F0.imprint","IMPRINT",EDGE,{"derivedFrom":sQuery(id+"F0.wireOp",EDGE,"E158")}),-1.0]])]});
            var Q14;
            Q14=makeQuery(id+"F0.imprint","IMPRINT",FACE,{"disambiguationData":[TD([[makeQuery(id+"F0.imprint","IMPRINT",EDGE,{"derivedFrom":sQuery(id+"F0.wireOp",EDGE,"E180")}),-1.0]])]});
            var Q15;
            {var subQ3=sQuery(id+"F0.wireOp",EDGE,"E2");Q15=makeQuery(id+"F0.imprint","IMPRINT",FACE,{"disambiguationData":[TD([[makeQuery(id+"F0.imprint","IMPRINT",EDGE,{"derivedFrom":subQ3}),1.0]])]});}
            var Q16;
            Q16=makeQuery(id+"F0.imprint","IMPRINT",FACE,{"disambiguationData":[TD([[makeQuery(id+"F0.imprint","IMPRINT",EDGE,{"derivedFrom":sQuery(id+"F0.wireOp",EDGE,"E83")}),1.0]])]});
            var Q17;
            Q17=makeQuery(id+"F0.imprint","IMPRINT",FACE,{"disambiguationData":[TD([[makeQuery(id+"F0.imprint","IMPRINT",EDGE,{"derivedFrom":sQuery(id+"F0.wireOp",EDGE,"E200")}),-1.0]])]});
            var Q18;
            {var subQ0=sQuery(id+"F0.wireOp",EDGE,"E220");Q18=makeQuery(id+"F0.imprint","IMPRINT",FACE,{"disambiguationData":[TD([[makeQuery(id+"F0.imprint","IMPRINT",EDGE,{"derivedFrom":subQ0}),-1.0]])]});}
            var Q19;
            {var subQ0=sQuery(id+"F0.wireOp",EDGE,"E130");Q19=makeQuery(id+"F0.imprint","IMPRINT",FACE,{"disambiguationData":[TD([[makeQuery(id+"F0.imprint","IMPRINT",EDGE,{"derivedFrom":subQ0}),-1.0]])]});}
            var Q20;
            {var subQ3=sQuery(id+"F0.wireOp",EDGE,"E157");Q20=makeQuery(id+"F0.imprint","IMPRINT",FACE,{"disambiguationData":[TD([[makeQuery(id+"F0.imprint","IMPRINT",EDGE,{"derivedFrom":subQ3}),-1.0]])]});}
            var Q21;
            {var subQ2=sQuery(id+"F0.wireOp",EDGE,"E124");Q21=makeQuery(id+"F0.imprint","IMPRINT",FACE,{"disambiguationData":[TD([[makeQuery(id+"F0.imprint","IMPRINT",EDGE,{"derivedFrom":subQ2}),-1.0]])]});}
            var Q22;
            Q22=makeQuery(id+"F0.imprint","IMPRINT",FACE,{"disambiguationData":[TD([[makeQuery(id+"F0.imprint","IMPRINT",EDGE,{"derivedFrom":sQuery(id+"F0.wireOp",EDGE,"E9")}),1.0]])]});
            var Q23;
            Q23=makeQuery(id+"F0.imprint","IMPRINT",FACE,{"disambiguationData":[TD([[makeQuery(id+"F0.imprint","IMPRINT",EDGE,{"derivedFrom":sQuery(id+"F0.wireOp",EDGE,"E149")}),-1.0]])]});
            var Q24;
            {var subQ2=sQuery(id+"F0.wireOp",EDGE,"E208");Q24=makeQuery(id+"F0.imprint","IMPRINT",FACE,{"disambiguationData":[TD([[makeQuery(id+"F0.imprint","IMPRINT",EDGE,{"derivedFrom":subQ2}),1.0]])]});}
            var Q25;
            {var subQ0=sQuery(id+"F0.wireOp",EDGE,"E176");Q25=makeQuery(id+"F0.imprint","IMPRINT",FACE,{"disambiguationData":[TD([[makeQuery(id+"F0.imprint","IMPRINT",EDGE,{"derivedFrom":subQ0}),1.0]])]});}
            var Q26;
            Q26=makeQuery(id+"F0.imprint","IMPRINT",FACE,{"disambiguationData":[TD([[makeQuery(id+"F0.imprint","IMPRINT",EDGE,{"derivedFrom":sQuery(id+"F0.wireOp",EDGE,"E242")}),-1.0]])]});
            var Q27;
            {var subQ3=sQuery(id+"F0.wireOp",EDGE,"E57");Q27=makeQuery(id+"F0.imprint","IMPRINT",FACE,{"disambiguationData":[TD([[makeQuery(id+"F0.imprint","IMPRINT",EDGE,{"derivedFrom":subQ3}),-1.0]])]});}
            var Q28;
            {var subQ0=sQuery(id+"F0.wireOp",EDGE,"E183");Q28=makeQuery(id+"F0.imprint","IMPRINT",FACE,{"disambiguationData":[TD([[makeQuery(id+"F0.imprint","IMPRINT",EDGE,{"derivedFrom":subQ0}),1.0]])]});}
            var Q29;
            {var subQ3=sQuery(id+"F0.wireOp",EDGE,"E152");Q29=makeQuery(id+"F0.imprint","IMPRINT",FACE,{"disambiguationData":[TD([[makeQuery(id+"F0.imprint","IMPRINT",EDGE,{"derivedFrom":subQ3}),-1.0]])]});}
            var Q30;
            Q30=makeQuery(id+"F0.imprint","IMPRINT",FACE,{"disambiguationData":[TD([[makeQuery(id+"F0.imprint","IMPRINT",EDGE,{"derivedFrom":sQuery(id+"F0.wireOp",EDGE,"E132")}),-1.0]])]});
            var Q31;
            Q31=makeQuery(id+"F0.imprint","IMPRINT",FACE,{"disambiguationData":[TD([[makeQuery(id+"F0.imprint","IMPRINT",EDGE,{"derivedFrom":sQuery(id+"F0.wireOp",EDGE,"E162")}),-1.0]])]});
            var Q32;
            Q32=makeQuery(id+"F0.imprint","IMPRINT",FACE,{"disambiguationData":[TD([[makeQuery(id+"F0.imprint","IMPRINT",EDGE,{"derivedFrom":sQuery(id+"F0.wireOp",EDGE,"E27")}),-1.0]])]});
            var Q33;
            Q33=makeQuery(id+"F0.imprint","IMPRINT",FACE,{"disambiguationData":[TD([[makeQuery(id+"F0.imprint","IMPRINT",EDGE,{"derivedFrom":sQuery(id+"F0.wireOp",EDGE,"E224")}),-1.0]])]});
            var Q34;
            {var subQ0=sQuery(id+"F0.wireOp",EDGE,"E203");Q34=makeQuery(id+"F0.imprint","IMPRINT",FACE,{"disambiguationData":[TD([[makeQuery(id+"F0.imprint","IMPRINT",EDGE,{"derivedFrom":subQ0}),1.0]])]});}
            var Q35;
            {var subQ0=sQuery(id+"F0.wireOp",EDGE,"E58");Q35=makeQuery(id+"F0.imprint","IMPRINT",FACE,{"disambiguationData":[TD([[makeQuery(id+"F0.imprint","IMPRINT",EDGE,{"derivedFrom":subQ0}),-1.0]])]});}
            var Q36;
            {var subQ3=sQuery(id+"F0.wireOp",EDGE,"E59");Q36=makeQuery(id+"F0.imprint","IMPRINT",FACE,{"disambiguationData":[TD([[makeQuery(id+"F0.imprint","IMPRINT",EDGE,{"derivedFrom":subQ3}),1.0]])]});}
            var Q37;
            {var subQ1=sQuery(id+"F0.wireOp",EDGE,"E221");Q37=makeQuery(id+"F0.imprint","IMPRINT",FACE,{"disambiguationData":[TD([[makeQuery(id+"F0.imprint","IMPRINT",EDGE,{"derivedFrom":subQ1}),1.0]])]});}
            var Q38;
            Q38=makeQuery(id+"F0.imprint","IMPRINT",FACE,{"disambiguationData":[TD([[makeQuery(id+"F0.imprint","IMPRINT",EDGE,{"derivedFrom":sQuery(id+"F0.wireOp",EDGE,"E28")}),-1.0]])]});
            var Q39;
            {var subQ3=sQuery(id+"F0.wireOp",EDGE,"E284");Q39=makeQuery(id+"F0.imprint","IMPRINT",FACE,{"disambiguationData":[TD([[makeQuery(id+"F0.imprint","IMPRINT",EDGE,{"derivedFrom":subQ3}),1.0]])]});}
            var Q40;
            Q40=makeQuery(id+"F0.imprint","IMPRINT",FACE,{"disambiguationData":[TD([[makeQuery(id+"F0.imprint","IMPRINT",EDGE,{"derivedFrom":sQuery(id+"F0.wireOp",EDGE,"E237")}),-1.0]])]});
            var Q41;
            {var subQ1=sQuery(id+"F0.wireOp",EDGE,"E63");Q41=makeQuery(id+"F0.imprint","IMPRINT",FACE,{"disambiguationData":[TD([[makeQuery(id+"F0.imprint","IMPRINT",EDGE,{"derivedFrom":subQ1}),-1.0]])]});}
            var Q42;
            {var subQ1=sQuery(id+"F0.wireOp",EDGE,"E202");Q42=makeQuery(id+"F0.imprint","IMPRINT",FACE,{"disambiguationData":[TD([[makeQuery(id+"F0.imprint","IMPRINT",EDGE,{"derivedFrom":subQ1}),-1.0]])]});}
            var Q43;
            {var subQ0=sQuery(id+"F0.wireOp",EDGE,"E54");Q43=makeQuery(id+"F0.imprint","IMPRINT",FACE,{"disambiguationData":[TD([[makeQuery(id+"F0.imprint","IMPRINT",EDGE,{"derivedFrom":subQ0}),-1.0]])]});}
            var Q44;
            Q44=makeQuery(id+"F0.imprint","IMPRINT",FACE,{"disambiguationData":[TD([[makeQuery(id+"F0.imprint","IMPRINT",EDGE,{"derivedFrom":sQuery(id+"F0.wireOp",EDGE,"E165")}),-1.0]])]});
            var Q45;
            Q45=makeQuery(id+"F0.imprint","IMPRINT",FACE,{"disambiguationData":[TD([[makeQuery(id+"F0.imprint","IMPRINT",EDGE,{"derivedFrom":sQuery(id+"F0.wireOp",EDGE,"E200")}),1.0]])]});
            var Q46;
            Q46=makeQuery(id+"F0.imprint","IMPRINT",FACE,{"disambiguationData":[TD([[makeQuery(id+"F0.imprint","IMPRINT",EDGE,{"derivedFrom":sQuery(id+"F0.wireOp",EDGE,"E23")}),1.0]])]});
            var Q47;
            {var subQ0=sQuery(id+"F0.wireOp",EDGE,"E178");Q47=makeQuery(id+"F0.imprint","IMPRINT",FACE,{"disambiguationData":[TD([[makeQuery(id+"F0.imprint","IMPRINT",EDGE,{"derivedFrom":subQ0}),-1.0]])]});}
            var Q48;
            Q48=makeQuery(id+"F0.imprint","IMPRINT",FACE,{"disambiguationData":[TD([[makeQuery(id+"F0.imprint","IMPRINT",EDGE,{"derivedFrom":sQuery(id+"F0.wireOp",EDGE,"E71")}),1.0]])]});
            var Q49;
            {var subQ5=sQuery(id+"F0.wireOp",EDGE,"E56");Q49=makeQuery(id+"F0.imprint","IMPRINT",FACE,{"disambiguationData":[TD([[makeQuery(id+"F0.imprint","IMPRINT",EDGE,{"derivedFrom":subQ5}),1.0]])]});}
            var Q50;
            Q50=makeQuery(id+"F0.imprint","IMPRINT",FACE,{"disambiguationData":[TD([[makeQuery(id+"F0.imprint","IMPRINT",EDGE,{"derivedFrom":sQuery(id+"F0.wireOp",EDGE,"E19")}),1.0]])]});
            var Q51;
            Q51=makeQuery(id+"F0.imprint","IMPRINT",FACE,{"disambiguationData":[TD([[makeQuery(id+"F0.imprint","IMPRINT",EDGE,{"derivedFrom":sQuery(id+"F0.wireOp",EDGE,"E210")}),1.0]])]});
            var Q52;
            {var subQ2=sQuery(id+"F0.wireOp",EDGE,"E115");Q52=makeQuery(id+"F0.imprint","IMPRINT",FACE,{"disambiguationData":[TD([[makeQuery(id+"F0.imprint","IMPRINT",EDGE,{"derivedFrom":subQ2}),-1.0]])]});}
            var Q53;
            Q53=makeQuery(id+"F0.imprint","IMPRINT",FACE,{"disambiguationData":[TD([[makeQuery(id+"F0.imprint","IMPRINT",EDGE,{"derivedFrom":sQuery(id+"F0.wireOp",EDGE,"E51")}),-1.0]])]});
            var Q54;
            {var subQ1=sQuery(id+"F0.wireOp",EDGE,"E108");Q54=makeQuery(id+"F0.imprint","IMPRINT",FACE,{"disambiguationData":[TD([[makeQuery(id+"F0.imprint","IMPRINT",EDGE,{"derivedFrom":subQ1}),-1.0]])]});}
            var Q55;
            Q55=makeQuery(id+"F0.imprint","IMPRINT",FACE,{"disambiguationData":[TD([[makeQuery(id+"F0.imprint","IMPRINT",EDGE,{"derivedFrom":sQuery(id+"F0.wireOp",EDGE,"E260")}),-1.0]])]});
            var Q56;
            {var subQ2=sQuery(id+"F0.wireOp",EDGE,"E155");Q56=makeQuery(id+"F0.imprint","IMPRINT",FACE,{"disambiguationData":[TD([[makeQuery(id+"F0.imprint","IMPRINT",EDGE,{"derivedFrom":subQ2}),1.0]])]});}
            var Q57;
            Q57=makeQuery(id+"F0.imprint","IMPRINT",FACE,{"disambiguationData":[TD([[makeQuery(id+"F0.imprint","IMPRINT",EDGE,{"derivedFrom":sQuery(id+"F0.wireOp",EDGE,"E187")}),1.0]])]});
            var Q58;
            Q58=makeQuery(id+"F0.imprint","IMPRINT",FACE,{"disambiguationData":[TD([[makeQuery(id+"F0.imprint","IMPRINT",EDGE,{"derivedFrom":sQuery(id+"F0.wireOp",EDGE,"E20")}),1.0]])]});
            var Q59;
            Q59=makeQuery(id+"F0.imprint","IMPRINT",FACE,{"disambiguationData":[TD([[makeQuery(id+"F0.imprint","IMPRINT",EDGE,{"derivedFrom":sQuery(id+"F0.wireOp",EDGE,"E185")}),-1.0]])]});
            var Q60;
            Q60=makeQuery(id+"F0.imprint","IMPRINT",FACE,{"disambiguationData":[TD([[makeQuery(id+"F0.imprint","IMPRINT",EDGE,{"derivedFrom":sQuery(id+"F0.wireOp",EDGE,"E32")}),-1.0]])]});
            var Q61;
            {var subQ4=sQuery(id+"F0.wireOp",EDGE,"E166");Q61=makeQuery(id+"F0.imprint","IMPRINT",FACE,{"disambiguationData":[TD([[makeQuery(id+"F0.imprint","IMPRINT",EDGE,{"derivedFrom":subQ4}),-1.0]])]});}
            var Q62;
            {var subQ0=sQuery(id+"F0.wireOp",EDGE,"E24");Q62=makeQuery(id+"F0.imprint","IMPRINT",FACE,{"disambiguationData":[TD([[makeQuery(id+"F0.imprint","IMPRINT",EDGE,{"derivedFrom":subQ0}),1.0]])]});}
            var Q63;
            Q63=makeQuery(id+"F0.imprint","IMPRINT",FACE,{"disambiguationData":[TD([[makeQuery(id+"F0.imprint","IMPRINT",EDGE,{"derivedFrom":sQuery(id+"F0.wireOp",EDGE,"E234")}),-1.0]])]});
            var Q64;
            Q64=makeQuery(id+"F0.imprint","IMPRINT",FACE,{"disambiguationData":[TD([[makeQuery(id+"F0.imprint","IMPRINT",EDGE,{"derivedFrom":sQuery(id+"F0.wireOp",EDGE,"E76")}),1.0]])]});
            var Q65;
            Q65=makeQuery(id+"F0.imprint","IMPRINT",FACE,{"disambiguationData":[TD([[makeQuery(id+"F0.imprint","IMPRINT",EDGE,{"derivedFrom":sQuery(id+"F0.wireOp",EDGE,"E204")}),1.0]])]});
            var Q66;
            {var subQ0=sQuery(id+"F0.wireOp",EDGE,"E55");Q66=makeQuery(id+"F0.imprint","IMPRINT",FACE,{"disambiguationData":[TD([[makeQuery(id+"F0.imprint","IMPRINT",EDGE,{"derivedFrom":subQ0}),-1.0]])]});}
            var Q67;
            {var subQ0=sQuery(id+"F0.wireOp",EDGE,"E66");Q67=makeQuery(id+"F0.imprint","IMPRINT",FACE,{"disambiguationData":[TD([[makeQuery(id+"F0.imprint","IMPRINT",EDGE,{"derivedFrom":subQ0}),1.0]])]});}
            var Q68;
            {var subQ0=sQuery(id+"F0.wireOp",EDGE,"E255");Q68=makeQuery(id+"F0.imprint","IMPRINT",FACE,{"disambiguationData":[TD([[makeQuery(id+"F0.imprint","IMPRINT",EDGE,{"derivedFrom":subQ0}),-1.0]])]});}
            var Q69;
            Q69=makeQuery(id+"F0.imprint","IMPRINT",FACE,{"disambiguationData":[TD([[makeQuery(id+"F0.imprint","IMPRINT",EDGE,{"derivedFrom":sQuery(id+"F0.wireOp",EDGE,"E36")}),-1.0]])]});
            var Q70;
            {var subQ0=sQuery(id+"F0.wireOp",EDGE,"E113");Q70=makeQuery(id+"F0.imprint","IMPRINT",FACE,{"disambiguationData":[TD([[makeQuery(id+"F0.imprint","IMPRINT",EDGE,{"derivedFrom":subQ0}),-1.0]])]});}
            var Q71;
            {var subQ1=sQuery(id+"F0.wireOp",EDGE,"E95");Q71=makeQuery(id+"F0.imprint","IMPRINT",FACE,{"disambiguationData":[TD([[makeQuery(id+"F0.imprint","IMPRINT",EDGE,{"derivedFrom":subQ1}),-1.0]])]});}
            var Q72;
            {var subQ3=sQuery(id+"F0.wireOp",EDGE,"E42");Q72=makeQuery(id+"F0.imprint","IMPRINT",FACE,{"disambiguationData":[TD([[makeQuery(id+"F0.imprint","IMPRINT",EDGE,{"derivedFrom":subQ3}),1.0]])]});}
            var Q73;
            {var subQ2=sQuery(id+"F0.wireOp",EDGE,"E61");Q73=makeQuery(id+"F0.imprint","IMPRINT",FACE,{"disambiguationData":[TD([[makeQuery(id+"F0.imprint","IMPRINT",EDGE,{"derivedFrom":subQ2}),-1.0]])]});}
            var Q74;
            Q74=makeQuery(id+"F0.imprint","IMPRINT",FACE,{"disambiguationData":[TD([[makeQuery(id+"F0.imprint","IMPRINT",EDGE,{"derivedFrom":sQuery(id+"F0.wireOp",EDGE,"E227")}),1.0]])]});
            var Q75;
            Q75=makeQuery(id+"F0.imprint","IMPRINT",FACE,{"disambiguationData":[TD([[makeQuery(id+"F0.imprint","IMPRINT",EDGE,{"derivedFrom":sQuery(id+"F0.wireOp",EDGE,"E215")}),-1.0]])]});
            var Q76;
            Q76=makeQuery(id+"F0.imprint","IMPRINT",FACE,{"disambiguationData":[TD([[makeQuery(id+"F0.imprint","IMPRINT",EDGE,{"derivedFrom":sQuery(id+"F0.wireOp",EDGE,"E3")}),1.0]])]});
            var Q77;
            {var subQ0=sQuery(id+"F0.wireOp",EDGE,"E195");Q77=makeQuery(id+"F0.imprint","IMPRINT",FACE,{"disambiguationData":[TD([[makeQuery(id+"F0.imprint","IMPRINT",EDGE,{"derivedFrom":subQ0}),-1.0]])]});}
            var Q78;
            {var subQ3=sQuery(id+"F0.wireOp",EDGE,"E70");Q78=makeQuery(id+"F0.imprint","IMPRINT",FACE,{"disambiguationData":[TD([[makeQuery(id+"F0.imprint","IMPRINT",EDGE,{"derivedFrom":subQ3}),1.0]])]});}
            var Q79;
            {var subQ0=sQuery(id+"F0.wireOp",EDGE,"E289");Q79=makeQuery(id+"F0.imprint","IMPRINT",FACE,{"disambiguationData":[TD([[makeQuery(id+"F0.imprint","IMPRINT",EDGE,{"derivedFrom":subQ0}),-1.0]])]});}
            var Q80;
            {var subQ0=sQuery(id+"F0.wireOp",EDGE,"E98");Q80=makeQuery(id+"F0.imprint","IMPRINT",FACE,{"disambiguationData":[TD([[makeQuery(id+"F0.imprint","IMPRINT",EDGE,{"derivedFrom":subQ0}),1.0]])]});}
            var Q81;
            Q81=makeQuery(id+"F0.imprint","IMPRINT",FACE,{"disambiguationData":[TD([[makeQuery(id+"F0.imprint","IMPRINT",EDGE,{"derivedFrom":sQuery(id+"F0.wireOp",EDGE,"E196")}),-1.0]])]});
            var Q82;
            {var subQ3=sQuery(id+"F0.wireOp",EDGE,"E292");Q82=makeQuery(id+"F0.imprint","IMPRINT",FACE,{"disambiguationData":[TD([[makeQuery(id+"F0.imprint","IMPRINT",EDGE,{"derivedFrom":subQ3}),-1.0]])]});}
            var Q83;
            {var subQ0=sQuery(id+"F0.wireOp",EDGE,"E292");Q83=makeQuery(id+"F0.imprint","IMPRINT",FACE,{"disambiguationData":[TD([[makeQuery(id+"F0.imprint","IMPRINT",EDGE,{"derivedFrom":subQ0}),1.0]])]});}
            var Q84;
            Q84=makeQuery(id+"F0.imprint","IMPRINT",FACE,{"disambiguationData":[TD([[makeQuery(id+"F0.imprint","IMPRINT",EDGE,{"derivedFrom":sQuery(id+"F0.wireOp",EDGE,"E225")}),-1.0]])]});
            var Q85;
            Q85=makeQuery(id+"F0.imprint","IMPRINT",FACE,{"disambiguationData":[TD([[makeQuery(id+"F0.imprint","IMPRINT",EDGE,{"derivedFrom":sQuery(id+"F0.wireOp",EDGE,"E4")}),1.0]])]});
            var Q86;
            Q86=makeQuery(id+"F0.imprint","IMPRINT",FACE,{"disambiguationData":[TD([[makeQuery(id+"F0.imprint","IMPRINT",EDGE,{"derivedFrom":sQuery(id+"F0.wireOp",EDGE,"E279")}),-1.0]])]});
            var Q87;
            Q87=makeQuery(id+"F0.imprint","IMPRINT",FACE,{"disambiguationData":[TD([[makeQuery(id+"F0.imprint","IMPRINT",EDGE,{"derivedFrom":sQuery(id+"F0.wireOp",EDGE,"E37")}),-1.0]])]});
            var Q88;
            {var subQ0=sQuery(id+"F0.wireOp",EDGE,"E171");Q88=makeQuery(id+"F0.imprint","IMPRINT",FACE,{"disambiguationData":[TD([[makeQuery(id+"F0.imprint","IMPRINT",EDGE,{"derivedFrom":subQ0}),1.0]])]});}
            var Q89;
            Q89=makeQuery(id+"F0.imprint","IMPRINT",FACE,{"disambiguationData":[TD([[makeQuery(id+"F0.imprint","IMPRINT",EDGE,{"derivedFrom":sQuery(id+"F0.wireOp",EDGE,"E147")}),1.0]])]});
            var Q90;
            {var subQ3=sQuery(id+"F0.wireOp",EDGE,"E294");Q90=makeQuery(id+"F0.imprint","IMPRINT",FACE,{"disambiguationData":[TD([[makeQuery(id+"F0.imprint","IMPRINT",EDGE,{"derivedFrom":subQ3}),-1.0]])]});}
            var Q91;
            {var subQ0=sQuery(id+"F0.wireOp",EDGE,"E102");Q91=makeQuery(id+"F0.imprint","IMPRINT",FACE,{"disambiguationData":[TD([[makeQuery(id+"F0.imprint","IMPRINT",EDGE,{"derivedFrom":subQ0}),-1.0]])]});}
            var Q92;
            Q92=makeQuery(id+"F0.imprint","IMPRINT",FACE,{"disambiguationData":[TD([[makeQuery(id+"F0.imprint","IMPRINT",EDGE,{"derivedFrom":sQuery(id+"F0.wireOp",EDGE,"E184")}),-1.0]])]});
            var Q93;
            {var subQ0=sQuery(id+"F0.wireOp",EDGE,"E257");Q93=makeQuery(id+"F0.imprint","IMPRINT",FACE,{"disambiguationData":[TD([[makeQuery(id+"F0.imprint","IMPRINT",EDGE,{"derivedFrom":subQ0}),1.0]])]});}
            var Q94;
            Q94=makeQuery(id+"F0.imprint","IMPRINT",FACE,{"disambiguationData":[TD([[makeQuery(id+"F0.imprint","IMPRINT",EDGE,{"derivedFrom":sQuery(id+"F0.wireOp",EDGE,"E193")}),1.0]])]});
            var Q95;
            Q95=makeQuery(id+"F0.imprint","IMPRINT",FACE,{"disambiguationData":[TD([[makeQuery(id+"F0.imprint","IMPRINT",EDGE,{"derivedFrom":sQuery(id+"F0.wireOp",EDGE,"E118")}),-1.0]])]});
            var Q96;
            {var subQ0=sQuery(id+"F0.wireOp",EDGE,"E254");Q96=makeQuery(id+"F0.imprint","IMPRINT",FACE,{"disambiguationData":[TD([[makeQuery(id+"F0.imprint","IMPRINT",EDGE,{"derivedFrom":subQ0}),-1.0]])]});}
            var Q97;
            Q97=makeQuery(id+"F0.imprint","IMPRINT",FACE,{"disambiguationData":[TD([[makeQuery(id+"F0.imprint","IMPRINT",EDGE,{"derivedFrom":sQuery(id+"F0.wireOp",EDGE,"E282")}),-1.0]])]});
            var Q98;
            Q98=makeQuery(id+"F0.imprint","IMPRINT",FACE,{"disambiguationData":[TD([[makeQuery(id+"F0.imprint","IMPRINT",EDGE,{"derivedFrom":sQuery(id+"F0.wireOp",EDGE,"E99")}),1.0]])]});
            var Q99;
            Q99=makeQuery(id+"F0.imprint","IMPRINT",FACE,{"disambiguationData":[TD([[makeQuery(id+"F0.imprint","IMPRINT",EDGE,{"derivedFrom":sQuery(id+"F0.wireOp",EDGE,"E10")}),1.0]])]});
            var Q100;
            Q100=makeQuery(id+"F0.imprint","IMPRINT",FACE,{"disambiguationData":[TD([[makeQuery(id+"F0.imprint","IMPRINT",EDGE,{"derivedFrom":sQuery(id+"F0.wireOp",EDGE,"E144")}),-1.0]])]});
            var Q101;
            Q101=makeQuery(id+"F0.imprint","IMPRINT",FACE,{"disambiguationData":[TD([[makeQuery(id+"F0.imprint","IMPRINT",EDGE,{"derivedFrom":sQuery(id+"F0.wireOp",EDGE,"E211")}),-1.0]])]});
            var Q102;
            {var subQ0=sQuery(id+"F0.wireOp",EDGE,"E72");Q102=makeQuery(id+"F0.imprint","IMPRINT",FACE,{"disambiguationData":[TD([[makeQuery(id+"F0.imprint","IMPRINT",EDGE,{"derivedFrom":subQ0}),-1.0]])]});}
            var Q103;
            Q103=makeQuery(id+"F0.imprint","IMPRINT",FACE,{"disambiguationData":[TD([[makeQuery(id+"F0.imprint","IMPRINT",EDGE,{"derivedFrom":sQuery(id+"F0.wireOp",EDGE,"E231")}),1.0]])]});
            var Q104;
            {var subQ0=sQuery(id+"F0.wireOp",EDGE,"E287");Q104=makeQuery(id+"F0.imprint","IMPRINT",FACE,{"disambiguationData":[TD([[makeQuery(id+"F0.imprint","IMPRINT",EDGE,{"derivedFrom":subQ0}),-1.0]])]});}
            var Q105;
            Q105=makeQuery(id+"F0.imprint","IMPRINT",FACE,{"disambiguationData":[TD([[makeQuery(id+"F0.imprint","IMPRINT",EDGE,{"derivedFrom":sQuery(id+"F0.wireOp",EDGE,"E172")}),-1.0]])]});
            var Q106;
            Q106=makeQuery(id+"F0.imprint","IMPRINT",FACE,{"disambiguationData":[TD([[makeQuery(id+"F0.imprint","IMPRINT",EDGE,{"derivedFrom":sQuery(id+"F0.wireOp",EDGE,"E170")}),-1.0]])]});
            var Q107;
            Q107=makeQuery(id+"F0.imprint","IMPRINT",FACE,{"disambiguationData":[TD([[makeQuery(id+"F0.imprint","IMPRINT",EDGE,{"derivedFrom":sQuery(id+"F0.wireOp",EDGE,"E45")}),-1.0]])]});
            var Q108;
            {var subQ0=sQuery(id+"F0.wireOp",EDGE,"E285");Q108=makeQuery(id+"F0.imprint","IMPRINT",FACE,{"disambiguationData":[TD([[makeQuery(id+"F0.imprint","IMPRINT",EDGE,{"derivedFrom":subQ0}),1.0]])]});}
            var Q109;
            {var subQ4=sQuery(id+"F0.wireOp",EDGE,"E8");Q109=makeQuery(id+"F0.imprint","IMPRINT",FACE,{"disambiguationData":[TD([[makeQuery(id+"F0.imprint","IMPRINT",EDGE,{"derivedFrom":subQ4}),1.0]])]});}
            var Q110;
            {var subQ2=sQuery(id+"F0.wireOp",EDGE,"E172");Q110=makeQuery(id+"F0.imprint","IMPRINT",FACE,{"disambiguationData":[TD([[makeQuery(id+"F0.imprint","IMPRINT",EDGE,{"derivedFrom":subQ2}),1.0]])]});}
            var Q111;
            Q111=makeQuery(id+"F0.imprint","IMPRINT",FACE,{"disambiguationData":[TD([[makeQuery(id+"F0.imprint","IMPRINT",EDGE,{"derivedFrom":sQuery(id+"F0.wireOp",EDGE,"E30")}),-1.0]])]});
            var Q112;
            {var subQ0=sQuery(id+"F0.wireOp",EDGE,"E259");Q112=makeQuery(id+"F0.imprint","IMPRINT",FACE,{"disambiguationData":[TD([[makeQuery(id+"F0.imprint","IMPRINT",EDGE,{"derivedFrom":subQ0}),-1.0]])]});}
            var Q113;
            {var subQ0=sQuery(id+"F0.wireOp",EDGE,"E116");Q113=makeQuery(id+"F0.imprint","IMPRINT",FACE,{"disambiguationData":[TD([[makeQuery(id+"F0.imprint","IMPRINT",EDGE,{"derivedFrom":subQ0}),-1.0]])]});}
            var Q114;
            Q114=makeQuery(id+"F0.imprint","IMPRINT",FACE,{"disambiguationData":[TD([[makeQuery(id+"F0.imprint","IMPRINT",EDGE,{"derivedFrom":sQuery(id+"F0.wireOp",EDGE,"E47")}),-1.0]])]});
            var Q115;
            {var subQ0=sQuery(id+"F0.wireOp",EDGE,"E69");Q115=makeQuery(id+"F0.imprint","IMPRINT",FACE,{"disambiguationData":[TD([[makeQuery(id+"F0.imprint","IMPRINT",EDGE,{"derivedFrom":subQ0}),-1.0]])]});}
            var Q116;
            {var subQ0=sQuery(id+"F0.wireOp",EDGE,"E192");Q116=makeQuery(id+"F0.imprint","IMPRINT",FACE,{"disambiguationData":[TD([[makeQuery(id+"F0.imprint","IMPRINT",EDGE,{"derivedFrom":subQ0}),-1.0]])]});}
            var Q117;
            {var subQ0=sQuery(id+"F0.wireOp",EDGE,"E139");Q117=makeQuery(id+"F0.imprint","IMPRINT",FACE,{"disambiguationData":[TD([[makeQuery(id+"F0.imprint","IMPRINT",EDGE,{"derivedFrom":subQ0}),-1.0]])]});}
            var Q118;
            {var subQ3=sQuery(id+"F0.wireOp",EDGE,"E104");Q118=makeQuery(id+"F0.imprint","IMPRINT",FACE,{"disambiguationData":[TD([[makeQuery(id+"F0.imprint","IMPRINT",EDGE,{"derivedFrom":subQ3}),-1.0]])]});}
            var Q119;
            Q119=makeQuery(id+"F0.imprint","IMPRINT",FACE,{"disambiguationData":[TD([[makeQuery(id+"F0.imprint","IMPRINT",EDGE,{"derivedFrom":sQuery(id+"F0.wireOp",EDGE,"E244")}),-1.0]])]});
            var Q120;
            {var subQ3=sQuery(id+"F0.wireOp",EDGE,"E142");Q120=makeQuery(id+"F0.imprint","IMPRINT",FACE,{"disambiguationData":[TD([[makeQuery(id+"F0.imprint","IMPRINT",EDGE,{"derivedFrom":subQ3}),1.0]])]});}
            var Q121;
            Q121=makeQuery(id+"F0.imprint","IMPRINT",FACE,{"disambiguationData":[TD([[makeQuery(id+"F0.imprint","IMPRINT",EDGE,{"derivedFrom":sQuery(id+"F0.wireOp",EDGE,"E240")}),-1.0]])]});
            var Q122;
            Q122=makeQuery(id+"F0.imprint","IMPRINT",FACE,{"disambiguationData":[TD([[makeQuery(id+"F0.imprint","IMPRINT",EDGE,{"derivedFrom":sQuery(id+"F0.wireOp",EDGE,"E228")}),1.0]])]});
            var Q123;
            Q123=makeQuery(id+"F0.imprint","IMPRINT",FACE,{"disambiguationData":[TD([[makeQuery(id+"F0.imprint","IMPRINT",EDGE,{"derivedFrom":sQuery(id+"F0.wireOp",EDGE,"E87")}),-1.0]])]});
            var Q124;
            Q124=makeQuery(id+"F0.imprint","IMPRINT",FACE,{"disambiguationData":[TD([[makeQuery(id+"F0.imprint","IMPRINT",EDGE,{"derivedFrom":sQuery(id+"F0.wireOp",EDGE,"E278")}),-1.0]])]});
            var Q125;
            {var subQ2=sQuery(id+"F0.wireOp",EDGE,"E140");Q125=makeQuery(id+"F0.imprint","IMPRINT",FACE,{"disambiguationData":[TD([[makeQuery(id+"F0.imprint","IMPRINT",EDGE,{"derivedFrom":subQ2}),1.0]])]});}
            var Q126;
            Q126=makeQuery(id+"F0.imprint","IMPRINT",FACE,{"disambiguationData":[TD([[makeQuery(id+"F0.imprint","IMPRINT",EDGE,{"derivedFrom":sQuery(id+"F0.wireOp",EDGE,"E103")}),-1.0]])]});
            var Q127;
            Q127=makeQuery(id+"F0.imprint","IMPRINT",FACE,{"disambiguationData":[TD([[makeQuery(id+"F0.imprint","IMPRINT",EDGE,{"derivedFrom":sQuery(id+"F0.wireOp",EDGE,"E88")}),-1.0]])]});
            var Q128;
            Q128=makeQuery(id+"F0.imprint","IMPRINT",FACE,{"disambiguationData":[TD([[makeQuery(id+"F0.imprint","IMPRINT",EDGE,{"derivedFrom":sQuery(id+"F0.wireOp",EDGE,"E250")}),-1.0]])]});
            var Q129;
            Q129=makeQuery(id+"F0.imprint","IMPRINT",FACE,{"disambiguationData":[TD([[makeQuery(id+"F0.imprint","IMPRINT",EDGE,{"derivedFrom":sQuery(id+"F0.wireOp",EDGE,"E249")}),-1.0]])]});
            var Q130;
            {var subQ0=sQuery(id+"F0.wireOp",EDGE,"E119");Q130=makeQuery(id+"F0.imprint","IMPRINT",FACE,{"disambiguationData":[TD([[makeQuery(id+"F0.imprint","IMPRINT",EDGE,{"derivedFrom":subQ0}),-1.0]])]});}
            var Q131;
            Q131=makeQuery(id+"F0.imprint","IMPRINT",FACE,{"disambiguationData":[TD([[makeQuery(id+"F0.imprint","IMPRINT",EDGE,{"derivedFrom":sQuery(id+"F0.wireOp",EDGE,"E251")}),-1.0]])]});
            var Q132;
            {var subQ0=sQuery(id+"F0.wireOp",EDGE,"E65");Q132=makeQuery(id+"F0.imprint","IMPRINT",FACE,{"disambiguationData":[TD([[makeQuery(id+"F0.imprint","IMPRINT",EDGE,{"derivedFrom":subQ0}),1.0]])]});}
            var Q133;
            Q133=makeQuery(id+"F0.imprint","IMPRINT",FACE,{"disambiguationData":[TD([[makeQuery(id+"F0.imprint","IMPRINT",EDGE,{"derivedFrom":sQuery(id+"F0.wireOp",EDGE,"E121")}),-1.0]])]});
            var Q134;
            Q134=makeQuery(id+"F0.imprint","IMPRINT",FACE,{"disambiguationData":[TD([[makeQuery(id+"F0.imprint","IMPRINT",EDGE,{"derivedFrom":sQuery(id+"F0.wireOp",EDGE,"E97")}),-1.0]])]});
            var Q135;
            Q135=makeQuery(id+"F0.imprint","IMPRINT",FACE,{"disambiguationData":[TD([[makeQuery(id+"F0.imprint","IMPRINT",EDGE,{"derivedFrom":sQuery(id+"F0.wireOp",EDGE,"E214")}),-1.0]])]});
            var Q136;
            Q136=makeQuery(id+"F0.imprint","IMPRINT",FACE,{"disambiguationData":[TD([[makeQuery(id+"F0.imprint","IMPRINT",EDGE,{"derivedFrom":sQuery(id+"F0.wireOp",EDGE,"E267")}),1.0]])]});
            var Q137;
            {var subQ1=sQuery(id+"F0.wireOp",EDGE,"E148");Q137=makeQuery(id+"F0.imprint","IMPRINT",FACE,{"disambiguationData":[TD([[makeQuery(id+"F0.imprint","IMPRINT",EDGE,{"derivedFrom":subQ1}),-1.0]])]});}
            var Q138;
            Q138=makeQuery(id+"F0.imprint","IMPRINT",FACE,{"disambiguationData":[TD([[makeQuery(id+"F0.imprint","IMPRINT",EDGE,{"derivedFrom":sQuery(id+"F0.wireOp",EDGE,"E271")}),-1.0]])]});
            var Q139;
            {var subQ0=sQuery(id+"F0.wireOp",EDGE,"E265");Q139=makeQuery(id+"F0.imprint","IMPRINT",FACE,{"disambiguationData":[TD([[makeQuery(id+"F0.imprint","IMPRINT",EDGE,{"derivedFrom":subQ0}),-1.0]])]});}
            var Q140;
            {var subQ2=sQuery(id+"F0.wireOp",EDGE,"E253");Q140=makeQuery(id+"F0.imprint","IMPRINT",FACE,{"disambiguationData":[TD([[makeQuery(id+"F0.imprint","IMPRINT",EDGE,{"derivedFrom":subQ2}),-1.0]])]});}
            var Q141;
            Q141=makeQuery(id+"F0.imprint","IMPRINT",FACE,{"disambiguationData":[TD([[makeQuery(id+"F0.imprint","IMPRINT",EDGE,{"derivedFrom":sQuery(id+"F0.wireOp",EDGE,"E262")}),-1.0]])]});
            var Q142;
            {var subQ3=sQuery(id+"F0.wireOp",EDGE,"E266");Q142=makeQuery(id+"F0.imprint","IMPRINT",FACE,{"disambiguationData":[TD([[makeQuery(id+"F0.imprint","IMPRINT",EDGE,{"derivedFrom":subQ3}),1.0]])]});}
            var Q143;
            {var subQ0=sQuery(id+"F0.wireOp",EDGE,"E137");Q143=makeQuery(id+"F0.imprint","IMPRINT",FACE,{"disambiguationData":[TD([[makeQuery(id+"F0.imprint","IMPRINT",EDGE,{"derivedFrom":subQ0}),1.0]])]});}
            var Q144;
            Q144=makeQuery(id+"F0.imprint","IMPRINT",FACE,{"disambiguationData":[TD([[makeQuery(id+"F0.imprint","IMPRINT",EDGE,{"derivedFrom":sQuery(id+"F0.wireOp",EDGE,"E117")}),1.0]])]});
            var Q145;
            {var subQ0=sQuery(id+"F0.wireOp",EDGE,"E248");Q145=makeQuery(id+"F0.imprint","IMPRINT",FACE,{"disambiguationData":[TD([[makeQuery(id+"F0.imprint","IMPRINT",EDGE,{"derivedFrom":subQ0}),1.0]])]});}
            var Q146;
            {var subQ3=sQuery(id+"F0.wireOp",EDGE,"E95");Q146=makeQuery(id+"F0.imprint","IMPRINT",FACE,{"disambiguationData":[TD([[makeQuery(id+"F0.imprint","IMPRINT",EDGE,{"derivedFrom":subQ3}),1.0]])]});}
            var Q147;
            Q147=makeQuery(id+"F0.imprint","IMPRINT",FACE,{"disambiguationData":[TD([[makeQuery(id+"F0.imprint","IMPRINT",EDGE,{"derivedFrom":sQuery(id+"F0.wireOp",EDGE,"E269")}),-1.0]])]});
            var Q148;
            {var subQ4=sQuery(id+"F0.wireOp",EDGE,"E277");Q148=makeQuery(id+"F0.imprint","IMPRINT",FACE,{"disambiguationData":[TD([[makeQuery(id+"F0.imprint","IMPRINT",EDGE,{"derivedFrom":subQ4}),1.0]])]});}
            var Q149;
            {var subQ3=sQuery(id+"F0.wireOp",EDGE,"E296.trimOffspring");Q149=makeQuery(id+"F0.imprint","IMPRINT",FACE,{"disambiguationData":[TD([[makeQuery(id+"F0.imprint","IMPRINT",EDGE,{"derivedFrom":subQ3}),-1.0]])]});}
            var Q150;
            {var subQ2=sQuery(id+"F0.wireOp",EDGE,"E277");Q150=makeQuery(id+"F0.imprint","IMPRINT",FACE,{"disambiguationData":[TD([[makeQuery(id+"F0.imprint","IMPRINT",EDGE,{"derivedFrom":subQ2}),-1.0]])]});}
            extrude(context, id + "F1", {"entities" : qUnion([Q0, Q1, Q2, Q3, Q4, Q5, Q6, Q7, Q8, Q9, Q10, Q11, Q12, Q13, Q14, Q15, Q16, Q17, Q18, Q19, Q20, Q21, Q22, Q23, Q24, Q25, Q26, Q27, Q28, Q29, Q30, Q31, Q32, Q33, Q34, Q35, Q36, Q37, Q38, Q39, Q40, Q41, Q42, Q43, Q44, Q45, Q46, Q47, Q48, Q49, Q50, Q51, Q52, Q53, Q54, Q55, Q56, Q57, Q58, Q59, Q60, Q61, Q62, Q63, Q64, Q65, Q66, Q67, Q68, Q69, Q70, Q71, Q72, Q73, Q74, Q75, Q76, Q77, Q78, Q79, Q80, Q81, Q82, Q83, Q84, Q85, Q86, Q87, Q88, Q89, Q90, Q91, Q92, Q93, Q94, Q95, Q96, Q97, Q98, Q99, Q100, Q101, Q102, Q103, Q104, Q105, Q106, Q107, Q108, Q109, Q110, Q111, Q112, Q113, Q114, Q115, Q116, Q117, Q118, Q119, Q120, Q121, Q122, Q123, Q124, Q125, Q126, Q127, Q128, Q129, Q130, Q131, Q132, Q133, Q134, Q135, Q136, Q137, Q138, Q139, Q140, Q141, Q142, Q143, Q144, Q145, Q146, Q147, Q148, Q149, Q150]), "oppositeDirection" : true, "depth" : 10 * mm, "offsetDistance" : 25 * mm});
        }
    });
